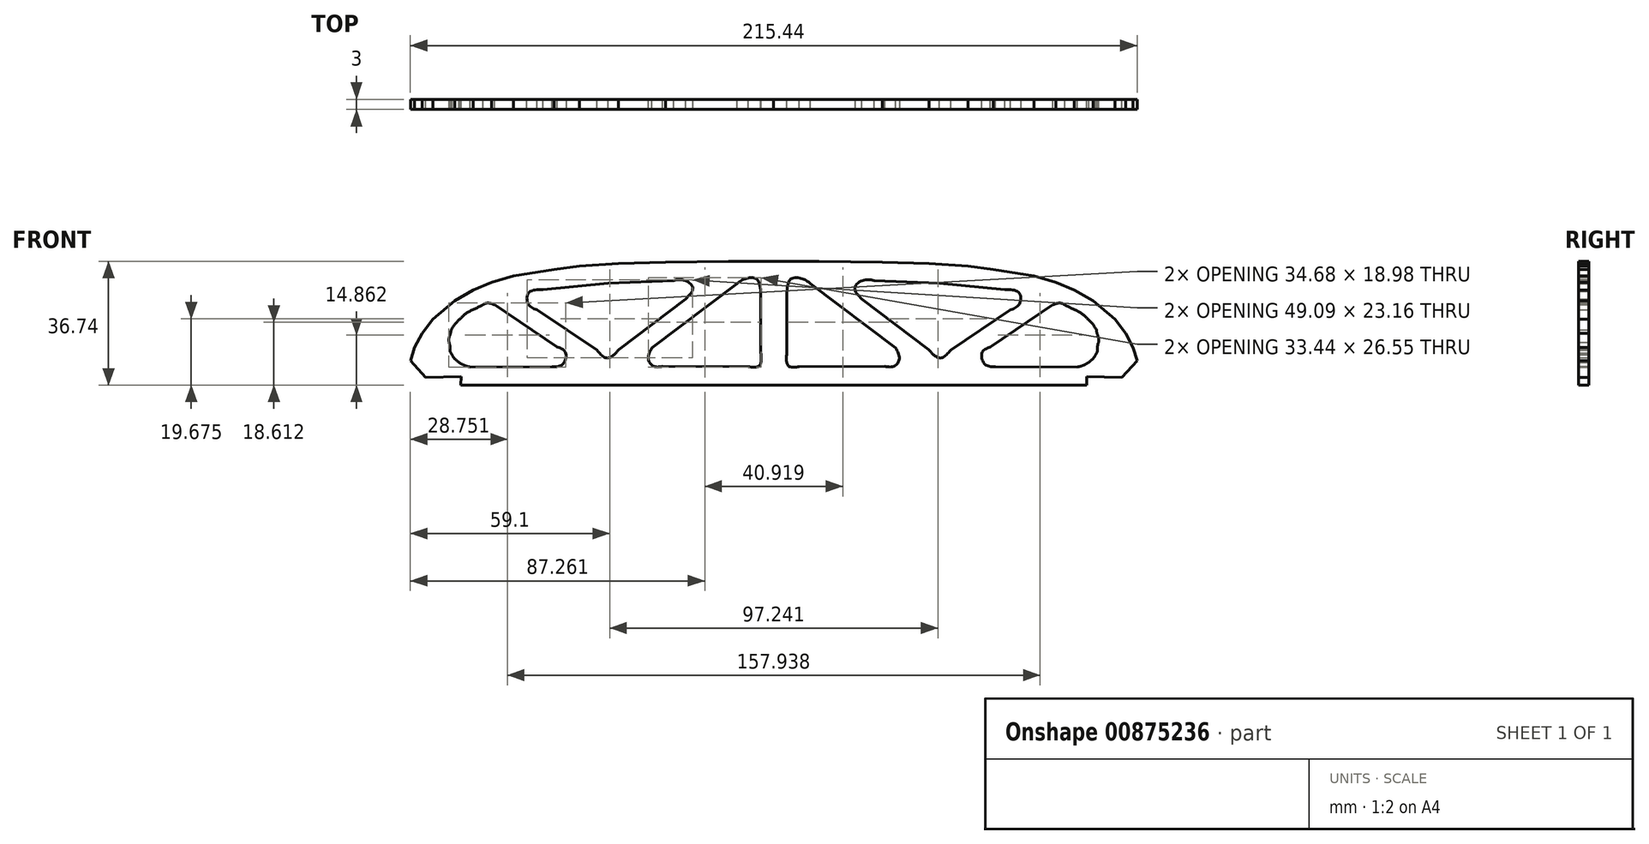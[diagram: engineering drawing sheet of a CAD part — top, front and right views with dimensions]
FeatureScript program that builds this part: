
annotation { "Feature Type Name" : "Feature", "Feature Type Description" : "" }
export const myFeature = defineFeature(function(context is Context, id is Id, definition is map)
    precondition{}
    {
        {
            var Q0;
            Q0=qCreatedBy(makeId("Front.planeOp"),FACE);
            var sketch = newSketch(context, id + "F0", { "sketchPlane" : qUnion([Q0])});
            skLineSegment(sketch, "E0", {"start": v(0, -18.36) * mm, "end": v(92.76, -18.37) * mm});
            skLineSegment(sketch, "E1", {"start": v(92.76, -18.37) * mm, "end": v(92.7, -15.9) * mm});
            skLineSegment(sketch, "E2", {"start": v(92.7, -15.9) * mm, "end": v(103.18, -16.1) * mm});
            skLineSegment(sketch, "E3", {"start": v(103.18, -16.1) * mm, "end": v(107.72, -11.14) * mm});
            skLineSegment(sketch, "E4", {"start": v(107.72, -11.14) * mm, "end": v(106.51, -7.17) * mm});
            skLineSegment(sketch, "E5", {"start": v(106.51, -7.17) * mm, "end": v(104.24, -3) * mm});
            skLineSegment(sketch, "E6", {"start": v(104.24, -3) * mm, "end": v(101.08, 1.13) * mm});
            skLineSegment(sketch, "E7", {"start": v(101.08, 1.13) * mm, "end": v(94.61, 6.6) * mm});
            skLineSegment(sketch, "E8", {"start": v(94.61, 6.6) * mm, "end": v(89.05, 9.82) * mm});
            skLineSegment(sketch, "E9", {"start": v(89.05, 9.82) * mm, "end": v(83.62, 12.1) * mm});
            skLineSegment(sketch, "E10", {"start": v(83.62, 12.1) * mm, "end": v(77.14, 14) * mm});
            skLineSegment(sketch, "E11", {"start": v(77.14, 14) * mm, "end": v(65.12, 15.93) * mm});
            skLineSegment(sketch, "E12", {"start": v(65.12, 15.93) * mm, "end": v(57.61, 16.92) * mm});
            skLineSegment(sketch, "E13", {"start": v(57.61, 16.92) * mm, "end": v(46, 17.74) * mm});
            skLineSegment(sketch, "E14", {"start": v(46, 17.74) * mm, "end": v(32.12, 18.07) * mm});
            skLineSegment(sketch, "E15", {"start": v(32.12, 18.07) * mm, "end": v(13.38, 18.27) * mm});
            skLineSegment(sketch, "E16", {"start": v(13.38, 18.27) * mm, "end": v(-0.05, 18.37) * mm});
            skLineSegment(sketch, "E17", {"start": v(-0.05, 18.37) * mm, "end": v(0, -18.36) * mm});
            skLineSegment(sketch, "E18", {"start": v(3.85, 9.45) * mm, "end": v(3.85, -8.8) * mm});
            skLineSegment(sketch, "E19", {"start": v(7.56, -12.9) * mm, "end": v(32.92, -12.8) * mm});
            skLineSegment(sketch, "E20", {"start": v(36.13, -7.29) * mm, "end": v(10.87, 11.76) * mm});
            skLineSegment(sketch, "E21", {"start": v(26.1, 7.15) * mm, "end": v(45.95, -7.79) * mm});
            skLineSegment(sketch, "E22", {"start": v(52.46, -7.99) * mm, "end": v(70.2, 3.94) * mm});
            skLineSegment(sketch, "E23", {"start": v(68.45, 10) * mm, "end": v(49.06, 11.88) * mm});
            skLineSegment(sketch, "E24", {"start": v(49.06, 11.88) * mm, "end": v(29.71, 12.66) * mm});
            skLineSegment(sketch, "E25", {"start": v(64.2, -7.09) * mm, "end": v(82.78, 5.44) * mm});
            skLineSegment(sketch, "E26", {"start": v(90, -13) * mm, "end": v(65.7, -12.9) * mm});
            skFitSpline(sketch, "E27", {"points": [v(3.85, -8.8) * mm, v(3.76, -11.05) * mm, v(4.47, -12.77) * mm, v(7.56, -12.9) * mm]});
            skFitSpline(sketch, "E28", {"points": [v(32.92, -12.8) * mm, v(35.7, -12.75) * mm, v(37.2, -10.57) * mm, v(36.13, -7.29) * mm]});
            skFitSpline(sketch, "E29", {"points": [v(10.87, 11.76) * mm, v(8.57, 13.14) * mm, v(5.16, 13.15) * mm, v(3.85, 9.45) * mm]});
            skFitSpline(sketch, "E30", {"points": [v(29.71, 12.66) * mm, v(26.63, 12.75) * mm, v(24.03, 10.48) * mm, v(26.1, 7.15) * mm]});
            skFitSpline(sketch, "E31", {"points": [v(45.95, -7.79) * mm, v(47.67, -9.6) * mm, v(49.68, -10.3) * mm, v(52.46, -7.99) * mm]});
            skFitSpline(sketch, "E32", {"points": [v(70.2, 3.94) * mm, v(72.78, 5.68) * mm, v(72.66, 9) * mm, v(68.45, 10) * mm]});
            skFitSpline(sketch, "E33", {"points": [v(82.78, 5.44) * mm, v(83.88, 5.84) * mm, v(85.01, 5.97) * mm, v(86.24, 5.44) * mm]});
            skFitSpline(sketch, "E34", {"points": [v(86.24, 5.44) * mm, v(88.59, 4.25) * mm, v(90.96, 3.08) * mm, v(92.66, 1.63) * mm]});
            skFitSpline(sketch, "E35", {"points": [v(92.66, 1.63) * mm, v(93.8, 0.5) * mm, v(94.73, -0.58) * mm, v(95.61, -1.98) * mm]});
            skFitSpline(sketch, "E36", {"points": [v(95.61, -1.98) * mm, v(95.86, -3.18) * mm, v(96.28, -4.48) * mm, v(96.26, -5.68) * mm]});
            skFitSpline(sketch, "E37", {"points": [v(96.26, -5.68) * mm, v(95.98, -6.9) * mm, v(95.9, -8.38) * mm, v(95.36, -9.34) * mm]});
            skFitSpline(sketch, "E38", {"points": [v(95.36, -9.34) * mm, v(94.85, -10.27) * mm, v(94.13, -10.93) * mm, v(93.36, -11.6) * mm]});
            skFitSpline(sketch, "E39", {"points": [v(93.36, -11.6) * mm, v(92.5, -12.14) * mm, v(91.13, -12.72) * mm, v(90, -13) * mm]});
            skFitSpline(sketch, "E40", {"points": [v(65.7, -12.9) * mm, v(62.56, -12.17) * mm, v(61.77, -8.7) * mm, v(64.2, -7.09) * mm]});
            skSolve(sketch);
        }
        {
            var Q0;
            Q0=makeQuery(id+"F0.imprint","IMPRINT",FACE,{"disambiguationData":[TD([[makeQuery(id+"F0.imprint","IMPRINT",EDGE,{"derivedFrom":sQuery(id+"F0.wireOp",EDGE,"E0")}),1.0]])]});
            extrude(context, id + "F1", {"entities" : qUnion([Q0]), "depth" : 3 * mm, "offsetDistance" : 25 * mm});
        }
        {
            var Q0;
            Q0=makeQuery(id+"F1.opExtrude","SWEPT_BODY",BODY,{"disambiguationData":[OSD([sQuery(id+"F0.wireOp",EDGE,"E0"),sQuery(id+"F0.wireOp",EDGE,"E1"),sQuery(id+"F0.wireOp",EDGE,"E2"),sQuery(id+"F0.wireOp",EDGE,"E3"),sQuery(id+"F0.wireOp",EDGE,"E4"),sQuery(id+"F0.wireOp",EDGE,"E5"),sQuery(id+"F0.wireOp",EDGE,"E6"),sQuery(id+"F0.wireOp",EDGE,"E7"),sQuery(id+"F0.wireOp",EDGE,"E8"),sQuery(id+"F0.wireOp",EDGE,"E9"),sQuery(id+"F0.wireOp",EDGE,"E10"),sQuery(id+"F0.wireOp",EDGE,"E11"),sQuery(id+"F0.wireOp",EDGE,"E12"),sQuery(id+"F0.wireOp",EDGE,"E13"),sQuery(id+"F0.wireOp",EDGE,"E14"),sQuery(id+"F0.wireOp",EDGE,"E15"),sQuery(id+"F0.wireOp",EDGE,"E16"),sQuery(id+"F0.wireOp",EDGE,"E17"),sQuery(id+"F0.wireOp",EDGE,"E18"),sQuery(id+"F0.wireOp",EDGE,"E19"),sQuery(id+"F0.wireOp",EDGE,"E20"),sQuery(id+"F0.wireOp",EDGE,"E21"),sQuery(id+"F0.wireOp",EDGE,"E22"),sQuery(id+"F0.wireOp",EDGE,"E23"),sQuery(id+"F0.wireOp",EDGE,"E24"),sQuery(id+"F0.wireOp",EDGE,"E25"),sQuery(id+"F0.wireOp",EDGE,"E26"),sQuery(id+"F0.wireOp",EDGE,"E27"),sQuery(id+"F0.wireOp",EDGE,"E28"),sQuery(id+"F0.wireOp",EDGE,"E29"),sQuery(id+"F0.wireOp",EDGE,"E30"),sQuery(id+"F0.wireOp",EDGE,"E31"),sQuery(id+"F0.wireOp",EDGE,"E32"),sQuery(id+"F0.wireOp",EDGE,"E33"),sQuery(id+"F0.wireOp",EDGE,"E34"),sQuery(id+"F0.wireOp",EDGE,"E35"),sQuery(id+"F0.wireOp",EDGE,"E36"),sQuery(id+"F0.wireOp",EDGE,"E37"),sQuery(id+"F0.wireOp",EDGE,"E38"),sQuery(id+"F0.wireOp",EDGE,"E39"),sQuery(id+"F0.wireOp",EDGE,"E40")])]});
            var Q1;
            Q1=qCreatedBy(makeId("Right.planeOp"),FACE);
            mirror(context, id + "F2", {"operationType" : NewBodyOperationType.ADD, "entities" : qUnion([Q0]), "mirrorPlane" : qUnion([Q1])});
        }
    });
